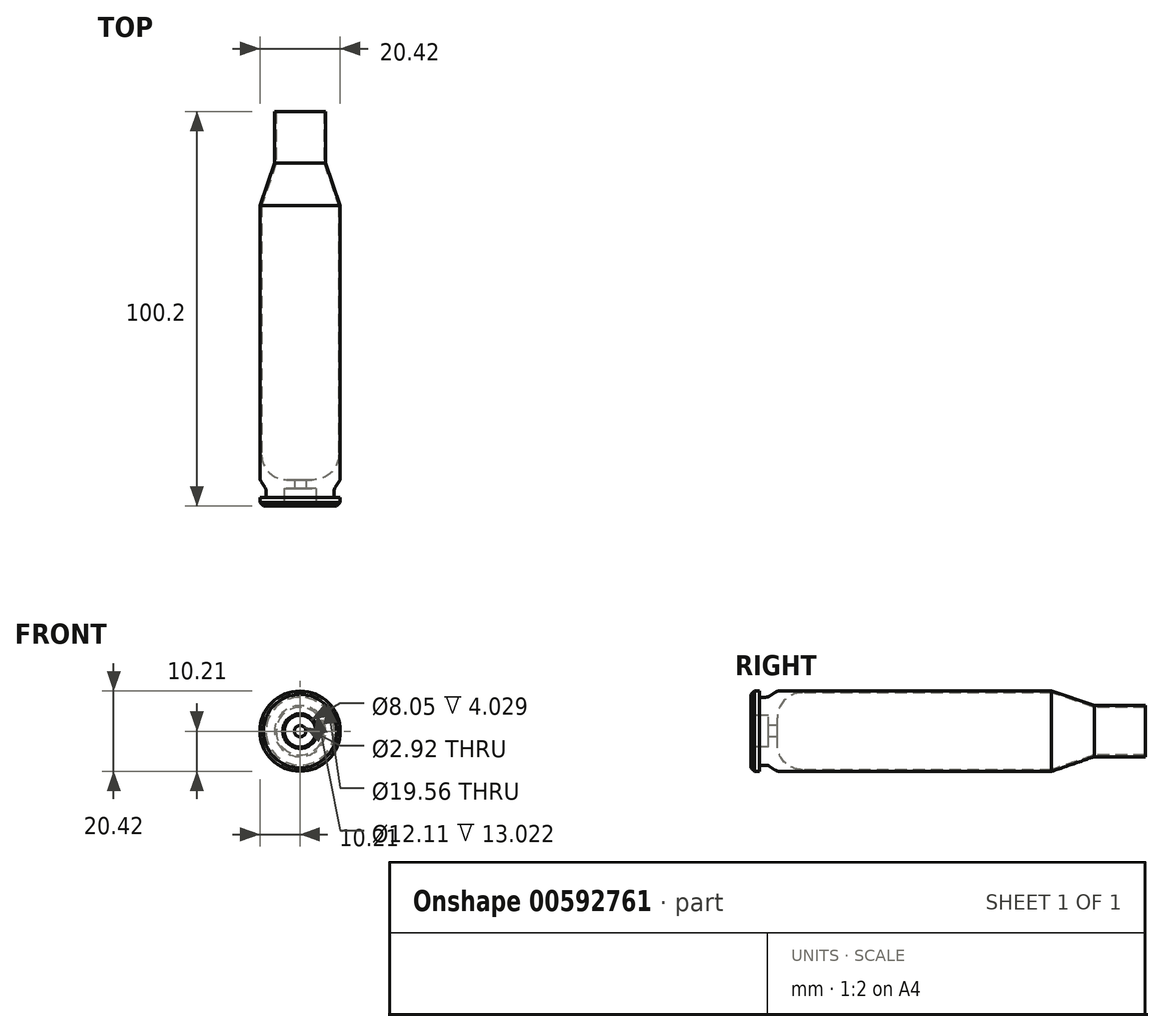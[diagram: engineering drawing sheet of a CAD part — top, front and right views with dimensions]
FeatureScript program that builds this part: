
annotation { "Feature Type Name" : "Feature", "Feature Type Description" : "" }
export const myFeature = defineFeature(function(context is Context, id is Id, definition is map)
    precondition{}
    {
        {
            var Q0;
            Q0=qCreatedBy(makeId("Right.planeOp"),FACE);
            var sketch = newSketch(context, id + "F0", { "sketchPlane" : qUnion([Q0])});
            skLineSegment(sketch, "E0", {"start": v(0, 0) * mm, "end": v(2.16, 0) * mm});
            skLineSegment(sketch, "E1", {"start": v(0, 4.02) * mm, "end": v(0, 10.21) * mm});
            skLineSegment(sketch, "E2", {"start": v(0, 10.21) * mm, "end": v(2.16, 10.21) * mm});
            skLineSegment(sketch, "E3", {"start": v(34.54, 55.63) * mm, "end": v(34.54, 55.63) * mm});
            skLineSegment(sketch, "E4", {"start": v(2.16, 8.64) * mm, "end": v(2.16, 10.21) * mm});
            skPoint(sketch, "E5.orphan", {"position": v(2.16, 0) * mm});
            skPoint(sketch, "E6.end.orphan", {"position": v(2.16, 5.1) * mm});
            skPoint(sketch, "E6.start.orphan", {"position": v(0, 5.1) * mm});
            skLineSegment(sketch, "E7", {"start": v(2.16, 8.64) * mm, "end": v(4.3, 8.64) * mm});
            skLineSegment(sketch, "E8", {"start": v(4.3, 8.64) * mm, "end": v(6.67, 10.21) * mm});
            skPoint(sketch, "E9.orphan", {"position": v(75.43, 0) * mm});
            skPoint(sketch, "E10.end.orphan", {"position": v(76.35, 0) * mm});
            skLineSegment(sketch, "E11", {"start": v(0, 22.27) * mm, "end": v(100.2, 22.27) * mm, "construction": true});
            skLineSegment(sketch, "E12", {"start": v(100.2, 6.49) * mm, "end": v(87.18, 6.49) * mm});
            skLineSegment(sketch, "E13", {"start": v(87.18, 6.49) * mm, "end": v(76.35, 10.21) * mm});
            skPoint(sketch, "E14.start.orphan", {"position": v(87.18, 0) * mm});
            skLineSegment(sketch, "E15", {"start": v(100.2, 6.49) * mm, "end": v(100.2, 6.06) * mm});
            skLineSegment(sketch, "E16", {"start": v(100.2, 6.06) * mm, "end": v(87.18, 6.06) * mm});
            skLineSegment(sketch, "E17", {"start": v(87.18, 6.06) * mm, "end": v(76.35, 9.78) * mm});
            skLineSegment(sketch, "E18", {"start": v(76.35, 9.78) * mm, "end": v(13.02, 9.78) * mm});
            skLineSegment(sketch, "E19", {"start": v(6.67, 3.43) * mm, "end": v(6.67, 1.46) * mm});
            skLineSegment(sketch, "E20", {"start": v(6.67, 1.46) * mm, "end": v(4.41, 1.46) * mm});
            skLineSegment(sketch, "E21", {"start": v(4.41, 1.46) * mm, "end": v(4.41, 4.02) * mm});
            skLineSegment(sketch, "E22", {"start": v(4.41, 4.02) * mm, "end": v(0, 4.02) * mm});
            skLineSegment(sketch, "E23.trimOffspring", {"start": v(6.67, 10.21) * mm, "end": v(76.35, 10.21) * mm});
            skPoint(sketch, "E24.visualSharp", {"position": v(6.67, 9.78) * mm});
            skArc(sketch, "E24.filletArc", {"start": v(13.02, 9.78) * mm, "mid": v(8.53, 7.92) * mm, "end": v(6.67, 3.43) * mm});
            skSolve(sketch);
        }
        {
            var Q0;
            Q0=makeQuery(id+"F0.imprint","IMPRINT",FACE,{"disambiguationData":[TD([[makeQuery(id+"F0.imprint","IMPRINT",EDGE,{"derivedFrom":sQuery(id+"F0.wireOp",EDGE,"E1")}),-1.0]])]});
            var Q1;
            Q1=sQuery(id+"F0.wireOp",EDGE,"E0");
            revolve(context, id + "F1", {"entities" : qUnion([Q0]), "axis" : qUnion([Q1]), "revolveType" : RevolveType.FULL});
        }
        {
            var Q0;
            Q0=makeQuery(id+"F1.opRevolve","SWEPT_EDGE",EDGE,{"disambiguationData":[OSD([sQuery(id+"F0.wireOp",EDGE,"E1"),sQuery(id+"F0.wireOp",EDGE,"E2")])]});
            chamfer(context, id + "F2", {"entities" : qUnion([Q0]), "width" : 0.89 * mm, "tangentPropagation" : true});
        }
        {
            var Q0;
            Q0=makeQuery(id+"F1.opRevolve","SWEPT_EDGE",EDGE,{"disambiguationData":[OSD([sQuery(id+"F0.wireOp",EDGE,"E1"),sQuery(id+"F0.wireOp",EDGE,"E22")])]});
            chamfer(context, id + "F3", {"entities" : qUnion([Q0]), "width" : 0.38 * mm, "tangentPropagation" : true});
        }
        {
            var Q0;
            Q0=makeQuery(id+"F1.opRevolve","SWEPT_EDGE",EDGE,{"disambiguationData":[OSD([sQuery(id+"F0.wireOp",EDGE,"E8"),sQuery(id+"F0.wireOp",EDGE,"E23.trimOffspring")])]});
            var Q1;
            Q1=makeQuery(id+"F1.opRevolve","SWEPT_EDGE",EDGE,{"disambiguationData":[OSD([sQuery(id+"F0.wireOp",EDGE,"E7"),sQuery(id+"F0.wireOp",EDGE,"E8")])]});
            fillet(context, id + "F4", {"entities" : qUnion([Q0, Q1]), "radius" : 1.65 * mm, "tangentPropagation" : true, "allowEdgeOverflow" : false});
        }
    });
